# Revit family: svetilnik_alfresco_fobos
name_source: partatom
category: Осветительные приборы
revit_build: Autodesk Revit 2016 (Build: 20150506_1715(x64)
units: mm (PartAtom-declared; Revit-internal decimal feet)

## family parameters
Всегда вертикально = Да
Источник света = Нет
На основе рабочей плоскости = Нет
Общий = Нет
При загрузке вырезать с полостями = Нет
Размер круглого соединителя = Использовать диаметр
Тип детали = Нормальный
Точка расчета площади = Нет

## types (3) — shared parameters
ADSK_Единица измерения = шт.
ADSK_Завод-изготовитель = ALFRESCO
ADSK_Количество фаз = 2
ADSK_Количество фаз числовое = 2
ADSK_Коэффициент мощности = 0.98
ADSK_Напряжение = 220 В
ADSK_Размер_Диаметр = 100 мм
ADSK_Ток = 0 А
ADSK_Энергоэффективность = 120 лм/Вт
IP Class = IP 67
URL = http://www.allfresco.ru
Блок аварийного питания = Нет
Изготовитель = ALFRESCO
Класс защиты = 1
Класс пожароопасности = F (светильники предназначены для установки непосредственно на поверхность из нормально воспламеняемых материалов)
Климатическая зона = У1
Корпус светильника = Антрацит
Материал рассеивателя = Закаленное противоударное стекло
Область использования = Любое общественное пространство от рекреационной зоны до городской площади
Отверстия под фланец = 190 мм
Отражатель = Отражатель
Рассеиватель = Стекло светильника
Светильник 1 = Да
Светильник 2 = Да
Светильник 3 = Да
Температура эксплуатации = -35 +40
Тип ИС = LED-светодиоды
Тип КСС = 60°
Тип ПРА = -
Тип продукции = LED-светильник
Тип светильника 4 = spot_04_10 : 18
Цветовая температура = 2700-6500
Ширина фланца = 230 мм

## per-type parameters (varying)
| type | ADSK_Артикул | ADSK_Масса | ADSK_Модель | ADSK_Наименование | ADSK_Номинальная мощность | ADSK_Полная мощность | ADSK_Размер_Высота | ADSK_Размер_Длина | ADSK_Размер_Ширина | Полная установленная мощность | Светильник 4 | Световой поток2 | Тип светильника 1 | Тип светильника 2 | Тип светильника 3 |
| ФОБОС А1 26Вт | 1135000110 | 34 | ФОБОС А1(SPOT-04М, ОКК 4,0-3) | ФОБОС А1 26Вт - св-ки SPOT-04М-AF 10Вт(60, 02, ЧМ) 2шт + 6Вт(60, 02, ЧМ) 1шт на опоре ОКК 4,0-3 оц+ЧМ | 26 Вт | 27 В·А | 4000 мм | 400 мм | 230 мм | 27 В·А | Нет | 3120 лм | spot_04_10 : 10 | spot_04_10 : 10 | spot_04_10 : 6 |
| ФОБОС А2 72Вт | 1130000640 | 57 | ФОБОС А2(SPOT-04Б, ОКК 6,0-4) | ФОБОС А2 72Вт - св-ки SPOT-04Б-AF 18Вт(60, 02, ЧМ) 4шт на опоре ОКК 6,0-4 оц+ЧМ | 72 Вт | 73 В·А | 6000 мм | 500 мм | 280 мм | 73 В·А | Да | 8640 лм | spot_04_10 : 18 | spot_04_10 : 18 | spot_04_10 : 18 |
| ФОБОС А3 84Вт | 1131000010 | 74 | ФОБОС А3(SPOT-04Б, ОКК 8,0-4) | ФОБОС А3 84Вт - св-ки SPOT-04Б-AF 18Вт(60, 02, ЧМ) 2шт + 24Вт(60, 02, ЧМ) 2шт на опоре ОКК 8,0-4 оц+ЧМ | 84 Вт | 86 В·А | 8000 мм | 500 мм | 280 мм | 86 В·А | Да | 10080 лм | spot_04_10 : 24 | spot_04_10 : 24 | spot_04_10 : 18 |

## geometry (parser evidence)
native form markers: Blend x2
no freeform markers — native parametric forms only
